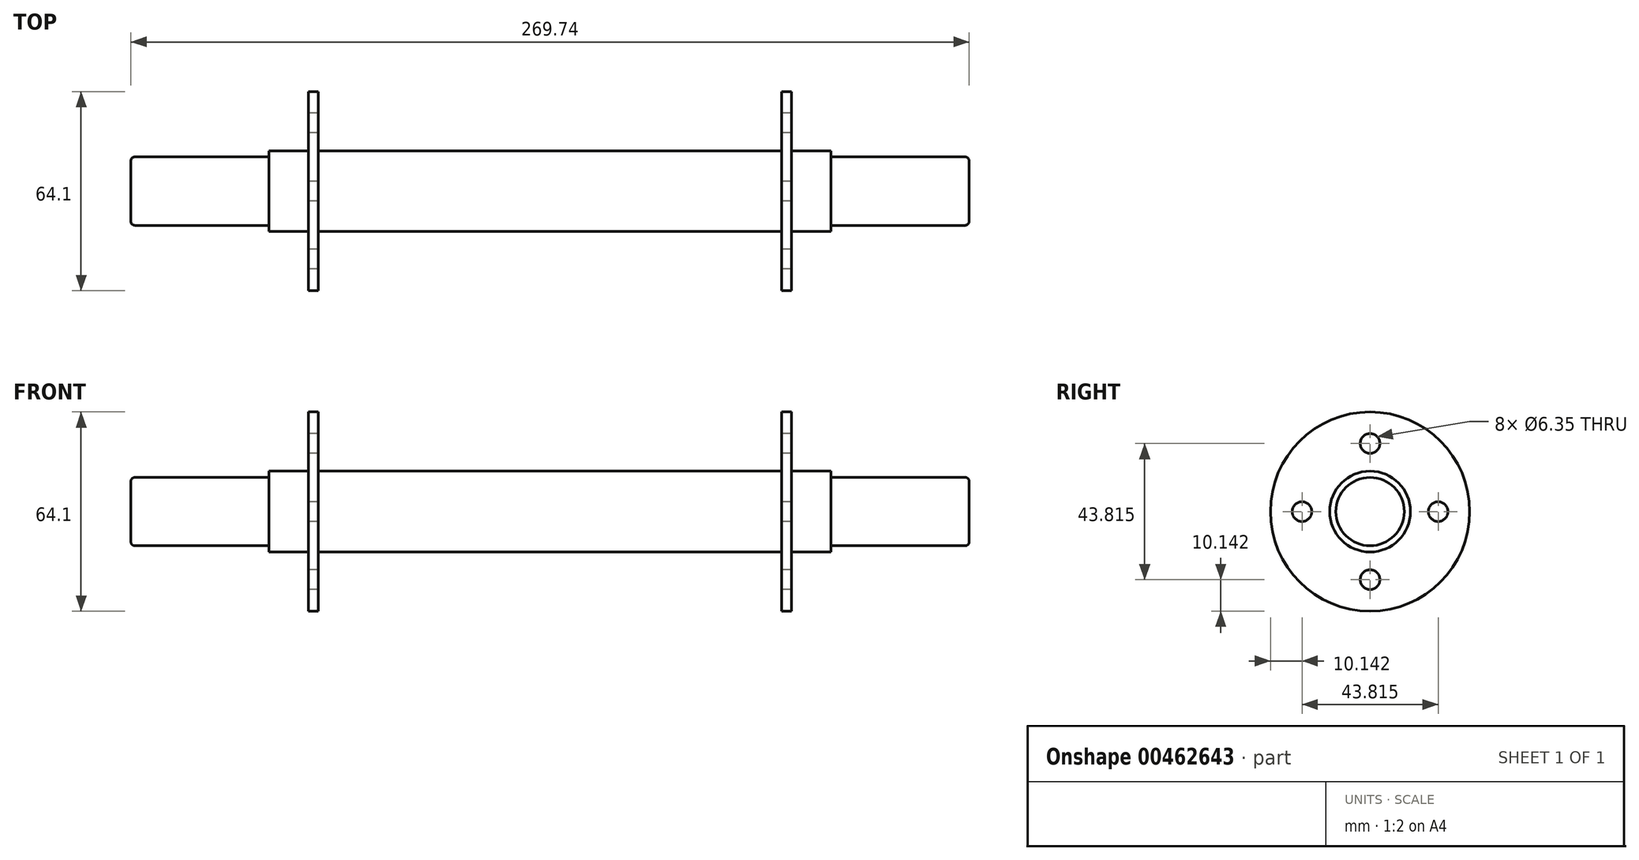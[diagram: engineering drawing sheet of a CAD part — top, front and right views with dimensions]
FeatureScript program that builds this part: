
annotation { "Feature Type Name" : "Feature", "Feature Type Description" : "" }
export const myFeature = defineFeature(function(context is Context, id is Id, definition is map)
    precondition{}
    {
        {
            var Q0;
            Q0=qCreatedBy(makeId("Front.planeOp"),FACE);
            var sketch = newSketch(context, id + "F0", { "sketchPlane" : qUnion([Q0])});
            skLineSegment(sketch, "E0", {"start": v(-166.23, 0) * mm, "end": v(149.9, 0) * mm, "construction": true});
            skLineSegment(sketch, "E1", {"start": v(-134.87, 0) * mm, "end": v(-134.87, 9.73) * mm});
            skLineSegment(sketch, "E2", {"start": v(-133.6, 11) * mm, "end": v(-90.42, 11) * mm});
            skLineSegment(sketch, "E3", {"start": v(-90.42, 11) * mm, "end": v(-90.42, 13) * mm});
            skLineSegment(sketch, "E4", {"start": v(-90.42, 13) * mm, "end": v(-77.72, 13) * mm});
            skLineSegment(sketch, "E5", {"start": v(90.42, 13) * mm, "end": v(90.42, 11) * mm});
            skLineSegment(sketch, "E6", {"start": v(90.42, 11) * mm, "end": v(133.6, 11) * mm});
            skLineSegment(sketch, "E7", {"start": v(134.87, 9.73) * mm, "end": v(134.87, 0) * mm});
            skLineSegment(sketch, "E8", {"start": v(134.87, 0) * mm, "end": v(-134.87, 0) * mm});
            skLineSegment(sketch, "E9", {"start": v(0, 0) * mm, "end": v(0, 70.44) * mm, "construction": true});
            skPoint(sketch, "E10.visualSharp", {"position": v(-134.87, 11) * mm});
            skArc(sketch, "E10.filletArc", {"start": v(-133.6, 11) * mm, "mid": v(-134.5, 10.63) * mm, "end": v(-134.87, 9.73) * mm});
            skPoint(sketch, "E11.visualSharp", {"position": v(134.87, 11) * mm});
            skArc(sketch, "E11.filletArc", {"start": v(134.87, 9.73) * mm, "mid": v(134.5, 10.63) * mm, "end": v(133.6, 11) * mm});
            skLineSegment(sketch, "E12.top", {"start": v(-77.72, 32.05) * mm, "end": v(-74.55, 32.05) * mm});
            skLineSegment(sketch, "E12.left", {"start": v(-77.72, 13) * mm, "end": v(-77.72, 32.05) * mm});
            skLineSegment(sketch, "E12.right", {"start": v(-74.55, 13) * mm, "end": v(-74.55, 32.05) * mm});
            skLineSegment(sketch, "E13.top", {"start": v(77.72, 32.05) * mm, "end": v(74.55, 32.05) * mm});
            skLineSegment(sketch, "E13.left", {"start": v(77.72, 13) * mm, "end": v(77.72, 32.05) * mm});
            skLineSegment(sketch, "E13.right", {"start": v(74.55, 13) * mm, "end": v(74.55, 32.05) * mm});
            skLineSegment(sketch, "E14.trimOffspring", {"start": v(77.72, 13) * mm, "end": v(90.42, 13) * mm});
            skLineSegment(sketch, "E15.trimOffspring", {"start": v(-74.55, 13) * mm, "end": v(74.55, 13) * mm});
            skSolve(sketch);
        }
        {
            var Q0;
            Q0=makeQuery(id+"F0.imprint","IMPRINT",FACE,{"disambiguationData":[TD([[makeQuery(id+"F0.imprint","IMPRINT",EDGE,{"derivedFrom":sQuery(id+"F0.wireOp",EDGE,"E1")}),-1.0]])]});
            var Q1;
            Q1=sQuery(id+"F0.wireOp",EDGE,"E0");
            revolve(context, id + "F1", {"entities" : qUnion([Q0]), "axis" : qUnion([Q1]), "revolveType" : RevolveType.FULL});
        }
        {
            var Q0;
            Q0=makeQuery(id+"F1.opRevolve","SWEPT_BODY",BODY,{"disambiguationData":[OSD([sQuery(id+"F0.wireOp",EDGE,"E1"),sQuery(id+"F0.wireOp",EDGE,"E2"),sQuery(id+"F0.wireOp",EDGE,"E3"),sQuery(id+"F0.wireOp",EDGE,"E4"),sQuery(id+"F0.wireOp",EDGE,"E5"),sQuery(id+"F0.wireOp",EDGE,"E6"),sQuery(id+"F0.wireOp",EDGE,"E7"),sQuery(id+"F0.wireOp",EDGE,"E8"),sQuery(id+"F0.wireOp",EDGE,"E10.filletArc"),sQuery(id+"F0.wireOp",EDGE,"E11.filletArc")])]});
            transform(context, id + "F2", {"entities" : qUnion([Q0]), "transformType" : TransformType.TRANSLATION_3D, "dx" : 0 * mm, "dy" : 0 * mm, "dz" : 0 * mm, "makeCopy" : true});
        }
        {
            var Q0;
            Q0=makeQuery(id+"F1.opRevolve","SWEPT_BODY",BODY,{"disambiguationData":[OSD([sQuery(id+"F0.wireOp",EDGE,"E1"),sQuery(id+"F0.wireOp",EDGE,"E2"),sQuery(id+"F0.wireOp",EDGE,"E3"),sQuery(id+"F0.wireOp",EDGE,"E4"),sQuery(id+"F0.wireOp",EDGE,"E5"),sQuery(id+"F0.wireOp",EDGE,"E6"),sQuery(id+"F0.wireOp",EDGE,"E7"),sQuery(id+"F0.wireOp",EDGE,"E8"),sQuery(id+"F0.wireOp",EDGE,"E10.filletArc"),sQuery(id+"F0.wireOp",EDGE,"E11.filletArc")])]});
            deleteBodies(context, id + "F3", {"entities" : qUnion([Q0])});
        }
        {
            var Q0;
            Q0=makeQuery(id+"F2.opPattern","COPY",BODY,{"derivedFrom":makeQuery(id+"F1.opRevolve","SWEPT_BODY",BODY,{"disambiguationData":[OSD([sQuery(id+"F0.wireOp",EDGE,"E1"),sQuery(id+"F0.wireOp",EDGE,"E2"),sQuery(id+"F0.wireOp",EDGE,"E3"),sQuery(id+"F0.wireOp",EDGE,"E4"),sQuery(id+"F0.wireOp",EDGE,"E5"),sQuery(id+"F0.wireOp",EDGE,"E6"),sQuery(id+"F0.wireOp",EDGE,"E7"),sQuery(id+"F0.wireOp",EDGE,"E8"),sQuery(id+"F0.wireOp",EDGE,"E10.filletArc"),sQuery(id+"F0.wireOp",EDGE,"E11.filletArc")])]}),"instanceName":"1"});
            transform(context, id + "F4", {"entities" : qUnion([Q0]), "transformType" : TransformType.TRANSLATION_3D, "dx" : 0 * mm, "dy" : 0 * mm, "dz" : 0 * mm, "makeCopy" : true});
        }
        {
            var Q0;
            Q0=makeQuery(id+"F2.opPattern","COPY",BODY,{"derivedFrom":makeQuery(id+"F1.opRevolve","SWEPT_BODY",BODY,{"disambiguationData":[OSD([sQuery(id+"F0.wireOp",EDGE,"E1"),sQuery(id+"F0.wireOp",EDGE,"E2"),sQuery(id+"F0.wireOp",EDGE,"E3"),sQuery(id+"F0.wireOp",EDGE,"E4"),sQuery(id+"F0.wireOp",EDGE,"E5"),sQuery(id+"F0.wireOp",EDGE,"E6"),sQuery(id+"F0.wireOp",EDGE,"E7"),sQuery(id+"F0.wireOp",EDGE,"E8"),sQuery(id+"F0.wireOp",EDGE,"E10.filletArc"),sQuery(id+"F0.wireOp",EDGE,"E11.filletArc")])]}),"instanceName":"1"});
            deleteBodies(context, id + "F5", {"entities" : qUnion([Q0])});
        }
        {
            var Q0;
            Q0=makeQuery(id+"F4.opPattern","COPY",FACE,{"derivedFrom":makeQuery(id+"F2.opPattern","COPY",FACE,{"derivedFrom":makeQuery(id+"F1.opRevolve","SWEPT_FACE",FACE,{"disambiguationData":[OSD([sQuery(id+"F0.wireOp",EDGE,"E12.left")])]}),"instanceName":"1"}),"instanceName":"1"});
            var sketch = newSketch(context, id + "F6", { "sketchPlane" : qUnion([Q0])});
            skCircle(sketch, "E16", {"center": v(0, 0) * mm, "radius": 21.9 * mm, "construction": true});
            skCircle(sketch, "E17", {"center": v(0, 21.9) * mm, "radius": 3.18 * mm});
            skCircle(sketch, "E18.1.0", {"center": v(-21.9, 0) * mm, "radius": 3.18 * mm});
            skCircle(sketch, "E18.2.0", {"center": v(0, -21.9) * mm, "radius": 3.18 * mm});
            skCircle(sketch, "E18.3.0", {"center": v(21.9, 0) * mm, "radius": 3.18 * mm});
            skSolve(sketch);
        }
        {
            var Q0;
            Q0 = qSketchRegion(id + "F6", true);
            extrude(context, id + "F7", {"entities" : qUnion([Q0]), "operationType" : NewBodyOperationType.REMOVE, "oppositeDirection" : true, "depth" : 177.8 * mm});
        }
    });
